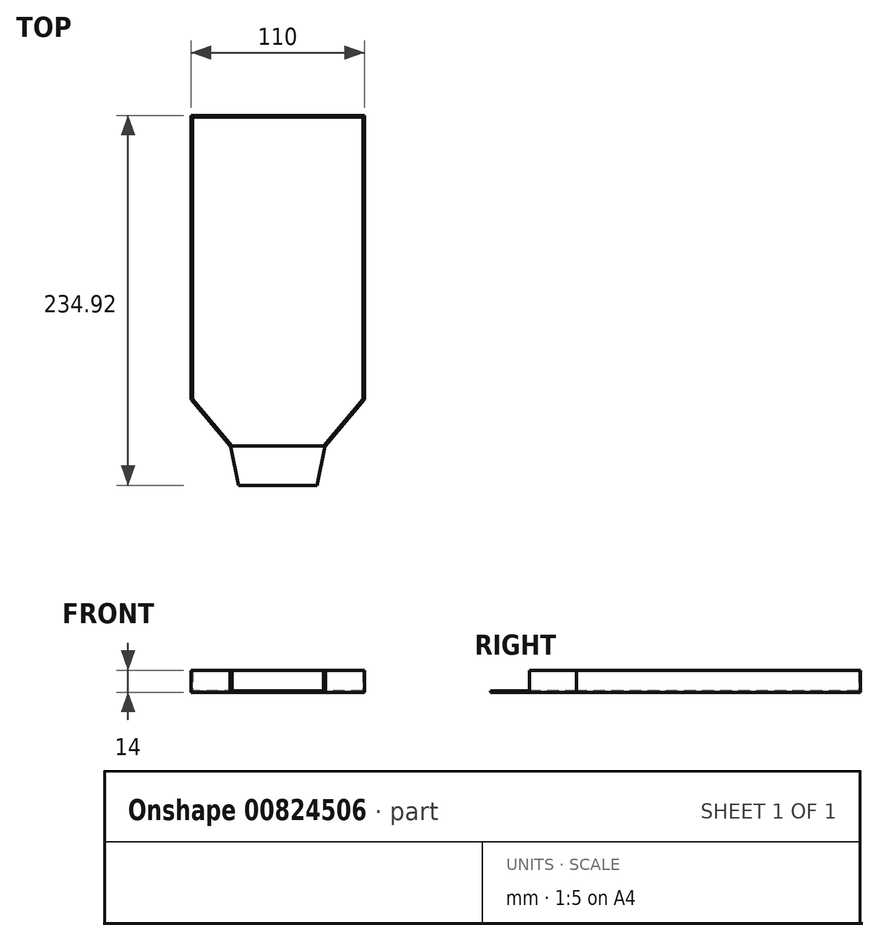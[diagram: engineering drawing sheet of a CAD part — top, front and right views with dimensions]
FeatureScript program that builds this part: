
annotation { "Feature Type Name" : "Feature", "Feature Type Description" : "" }
export const myFeature = defineFeature(function(context is Context, id is Id, definition is map)
    precondition{}
    {
        {
            var Q0;
            Q0=qCreatedBy(makeId("Top.planeOp"),FACE);
            var sketch = newSketch(context, id + "F0", { "sketchPlane" : qUnion([Q0])});
            skLineSegment(sketch, "E0.bottom", {"start": v(-58.97, 116.08) * mm, "end": v(51.03, 116.08) * mm});
            skLineSegment(sketch, "E0.top", {"start": v(-58.97, -93.92) * mm, "end": v(51.03, -93.92) * mm});
            skLineSegment(sketch, "E0.left", {"start": v(-58.97, 116.08) * mm, "end": v(-58.97, -93.92) * mm});
            skLineSegment(sketch, "E0.right", {"start": v(51.03, 116.08) * mm, "end": v(51.03, -93.92) * mm});
            skSolve(sketch);
        }
        {
            var Q0;
            Q0 = qSketchRegion(id + "F0", true);
            extrude(context, id + "F1", {"entities" : qUnion([Q0]), "depth" : 1 * mm, "offsetDistance" : 25 * mm});
        }
        {
            var Q0;
            Q0=makeQuery(id+"F1.opExtrude","CAP_FACE",FACE,{"disambiguationData":[OSD([sQuery(id+"F0.wireOp",EDGE,"E0.bottom"),sQuery(id+"F0.wireOp",EDGE,"E0.top"),sQuery(id+"F0.wireOp",EDGE,"E0.left"),sQuery(id+"F0.wireOp",EDGE,"E0.right")])],"isStart":false});
            var sketch = newSketch(context, id + "F2", { "sketchPlane" : qUnion([Q0])});
            skLineSegment(sketch, "E1.bottom", {"start": v(51.03, 116.08) * mm, "end": v(50.03, 116.08) * mm});
            skLineSegment(sketch, "E1.top", {"start": v(51.03, -93.92) * mm, "end": v(50.03, -93.92) * mm});
            skLineSegment(sketch, "E1.left", {"start": v(51.03, 116.08) * mm, "end": v(51.03, -93.92) * mm});
            skLineSegment(sketch, "E1.right", {"start": v(50.03, 116.08) * mm, "end": v(50.03, -93.92) * mm});
            skSolve(sketch);
        }
        {
            var Q0;
            Q0 = qSketchRegion(id + "F2", true);
            extrude(context, id + "F3", {"entities" : qUnion([Q0]), "operationType" : NewBodyOperationType.ADD, "depth" : 13 * mm, "offsetDistance" : 25 * mm});
        }
        {
            var Q0;
            Q0=makeQuery(id+"F1.opExtrude","CAP_FACE",FACE,{"disambiguationData":[OSD([sQuery(id+"F0.wireOp",EDGE,"E0.bottom"),sQuery(id+"F0.wireOp",EDGE,"E0.top"),sQuery(id+"F0.wireOp",EDGE,"E0.left"),sQuery(id+"F0.wireOp",EDGE,"E0.right")])],"isStart":false});
            var sketch = newSketch(context, id + "F4", { "sketchPlane" : qUnion([Q0])});
            skLineSegment(sketch, "E2.bottom", {"start": v(50.03, 116.08) * mm, "end": v(-58.97, 116.08) * mm});
            skLineSegment(sketch, "E2.top", {"start": v(50.03, 115.08) * mm, "end": v(-58.97, 115.08) * mm});
            skLineSegment(sketch, "E2.left", {"start": v(50.03, 116.08) * mm, "end": v(50.03, 115.08) * mm});
            skLineSegment(sketch, "E2.right", {"start": v(-58.97, 116.08) * mm, "end": v(-58.97, 115.08) * mm});
            skSolve(sketch);
        }
        {
            var Q0;
            Q0 = qSketchRegion(id + "F4", true);
            extrude(context, id + "F5", {"entities" : qUnion([Q0]), "operationType" : NewBodyOperationType.ADD, "depth" : 13 * mm, "offsetDistance" : 25 * mm});
        }
        {
            var Q0;
            Q0=makeQuery(id+"F1.opExtrude","CAP_FACE",FACE,{"disambiguationData":[OSD([sQuery(id+"F0.wireOp",EDGE,"E0.bottom"),sQuery(id+"F0.wireOp",EDGE,"E0.top"),sQuery(id+"F0.wireOp",EDGE,"E0.left"),sQuery(id+"F0.wireOp",EDGE,"E0.right")])],"isStart":false});
            var sketch = newSketch(context, id + "F6", { "sketchPlane" : qUnion([Q0])});
            skLineSegment(sketch, "E3.bottom", {"start": v(-58.97, 115.08) * mm, "end": v(-57.97, 115.08) * mm});
            skLineSegment(sketch, "E3.top", {"start": v(-58.97, -93.92) * mm, "end": v(-57.97, -93.92) * mm});
            skLineSegment(sketch, "E3.left", {"start": v(-58.97, 115.08) * mm, "end": v(-58.97, -93.92) * mm});
            skLineSegment(sketch, "E3.right", {"start": v(-57.97, 115.08) * mm, "end": v(-57.97, -93.92) * mm});
            skSolve(sketch);
        }
        {
            var Q0;
            Q0 = qSketchRegion(id + "F6", true);
            extrude(context, id + "F7", {"entities" : qUnion([Q0]), "operationType" : NewBodyOperationType.ADD, "depth" : 13 * mm, "offsetDistance" : 25 * mm});
        }
        {
            var Q0;
            Q0=makeQuery(id+"F1.opExtrude","CAP_FACE",FACE,{"disambiguationData":[OSD([sQuery(id+"F0.wireOp",EDGE,"E0.bottom"),sQuery(id+"F0.wireOp",EDGE,"E0.top"),sQuery(id+"F0.wireOp",EDGE,"E0.left"),sQuery(id+"F0.wireOp",EDGE,"E0.right")])],"isStart":false});
            var sketch = newSketch(context, id + "F8", { "sketchPlane" : qUnion([Q0])});
            skLineSegment(sketch, "E4", {"start": v(-32.97, -93.92) * mm, "end": v(-57.97, -93.92) * mm});
            skLineSegment(sketch, "E5", {"start": v(-57.97, -93.92) * mm, "end": v(-57.97, -63.92) * mm});
            skLineSegment(sketch, "E6", {"start": v(-57.97, -63.92) * mm, "end": v(-32.97, -93.92) * mm});
            skSolve(sketch);
        }
        {
            var Q0;
            Q0=makeQuery(id+"F8.imprint","IMPRINT",FACE,{"disambiguationData":[TD([[makeQuery(id+"F8.imprint","IMPRINT",EDGE,{"derivedFrom":sQuery(id+"F8.wireOp",EDGE,"E4")}),1.0]])]});
            extrude(context, id + "F9", {"entities" : qUnion([Q0]), "operationType" : NewBodyOperationType.ADD, "depth" : 13 * mm, "offsetDistance" : 25 * mm});
        }
        {
            var Q0;
            Q0=makeQuery(id+"F9.boolean.opBoolean","MERGE",FACE,{"derivedFrom":[makeQuery(id+"F7.boolean.opBoolean","MERGE",FACE,{"derivedFrom":[makeQuery(id+"F5.boolean.opBoolean","MERGE",FACE,{"derivedFrom":[makeQuery(id+"F3.opExtrude","CAP_FACE",FACE,{"disambiguationData":[OSD([sQuery(id+"F2.wireOp",EDGE,"E1.bottom"),sQuery(id+"F2.wireOp",EDGE,"E1.top"),sQuery(id+"F2.wireOp",EDGE,"E1.left"),sQuery(id+"F2.wireOp",EDGE,"E1.right")])],"isStart":false}),makeQuery(id+"F5.opExtrude","CAP_FACE",FACE,{"disambiguationData":[OSD([sQuery(id+"F4.wireOp",EDGE,"E2.bottom"),sQuery(id+"F4.wireOp",EDGE,"E2.top"),sQuery(id+"F4.wireOp",EDGE,"E2.left"),sQuery(id+"F4.wireOp",EDGE,"E2.right")])],"isStart":false})]}),makeQuery(id+"F7.opExtrude","CAP_FACE",FACE,{"disambiguationData":[OSD([sQuery(id+"F6.wireOp",EDGE,"E3.bottom"),sQuery(id+"F6.wireOp",EDGE,"E3.top"),sQuery(id+"F6.wireOp",EDGE,"E3.left"),sQuery(id+"F6.wireOp",EDGE,"E3.right")])],"isStart":false})]}),makeQuery(id+"F9.opExtrude","CAP_FACE",FACE,{"disambiguationData":[OSD([sQuery(id+"F8.wireOp",EDGE,"E4"),sQuery(id+"F8.wireOp",EDGE,"E5"),sQuery(id+"F8.wireOp",EDGE,"E6")])],"isStart":false})]});
            var Q1;
            Q1=makeQuery(id+"F9.boolean.opBoolean","MERGE",FACE,{"derivedFrom":[makeQuery(id+"F7.boolean.opBoolean","MERGE",FACE,{"derivedFrom":[makeQuery(id+"F3.boolean.opBoolean","MERGE",FACE,{"derivedFrom":[makeQuery(id+"F1.opExtrude","SWEPT_FACE",FACE,{"disambiguationData":[OSD([sQuery(id+"F0.wireOp",EDGE,"E0.top")])]}),makeQuery(id+"F3.opExtrude","SWEPT_FACE",FACE,{"disambiguationData":[OSD([sQuery(id+"F2.wireOp",EDGE,"E1.top")])]})]}),makeQuery(id+"F7.opExtrude","SWEPT_FACE",FACE,{"disambiguationData":[OSD([sQuery(id+"F6.wireOp",EDGE,"E3.top")])]})]}),makeQuery(id+"F9.opExtrude","SWEPT_FACE",FACE,{"disambiguationData":[OSD([sQuery(id+"F8.wireOp",EDGE,"E4")])]})]});
            var Q2;
            Q2=makeQuery(id+"F7.boolean.opBoolean","MERGE",FACE,{"derivedFrom":[makeQuery(id+"F5.boolean.opBoolean","MERGE",FACE,{"derivedFrom":[makeQuery(id+"F1.opExtrude","SWEPT_FACE",FACE,{"disambiguationData":[OSD([sQuery(id+"F0.wireOp",EDGE,"E0.left")])]}),makeQuery(id+"F5.opExtrude","SWEPT_FACE",FACE,{"disambiguationData":[OSD([sQuery(id+"F4.wireOp",EDGE,"E2.right")])]})]}),makeQuery(id+"F7.opExtrude","SWEPT_FACE",FACE,{"disambiguationData":[OSD([sQuery(id+"F6.wireOp",EDGE,"E3.left")])]})]});
            var Q3;
            Q3=makeQuery(id+"F1.opExtrude","CAP_FACE",FACE,{"disambiguationData":[OSD([sQuery(id+"F0.wireOp",EDGE,"E0.bottom"),sQuery(id+"F0.wireOp",EDGE,"E0.top"),sQuery(id+"F0.wireOp",EDGE,"E0.left"),sQuery(id+"F0.wireOp",EDGE,"E0.right")])],"isStart":true});
            shell(context, id + "F10", {"entities" : qUnion([Q0, Q1, Q2, Q3]), "thickness" : 1 * mm});
        }
        {
            var Q0;
            Q0=makeQuery(id+"F1.opExtrude","CAP_FACE",FACE,{"disambiguationData":[OSD([sQuery(id+"F0.wireOp",EDGE,"E0.bottom"),sQuery(id+"F0.wireOp",EDGE,"E0.top"),sQuery(id+"F0.wireOp",EDGE,"E0.left"),sQuery(id+"F0.wireOp",EDGE,"E0.right")])],"isStart":true});
            var sketch = newSketch(context, id + "F11", { "sketchPlane" : qUnion([Q0])});
            skSolve(sketch);
        }
        {
            var Q0;
            Q0=makeQuery(id+"F1.opExtrude","CAP_FACE",FACE,{"disambiguationData":[OSD([sQuery(id+"F0.wireOp",EDGE,"E0.bottom"),sQuery(id+"F0.wireOp",EDGE,"E0.top"),sQuery(id+"F0.wireOp",EDGE,"E0.left"),sQuery(id+"F0.wireOp",EDGE,"E0.right")])],"isStart":false});
            var sketch = newSketch(context, id + "F12", { "sketchPlane" : qUnion([Q0])});
            skLineSegment(sketch, "E7", {"start": v(50.03, -93.92) * mm, "end": v(25.03, -93.92) * mm});
            skLineSegment(sketch, "E8", {"start": v(50.03, -93.92) * mm, "end": v(50.03, -63.92) * mm});
            skLineSegment(sketch, "E9", {"start": v(50.03, -63.92) * mm, "end": v(25.03, -93.92) * mm});
            skSolve(sketch);
        }
        {
            var Q0;
            Q0=makeQuery(id+"F12.imprint","IMPRINT",FACE,{"disambiguationData":[TD([[makeQuery(id+"F12.imprint","IMPRINT",EDGE,{"derivedFrom":sQuery(id+"F12.wireOp",EDGE,"E7")}),1.0]])]});
            extrude(context, id + "F13", {"entities" : qUnion([Q0]), "operationType" : NewBodyOperationType.ADD, "depth" : 13 * mm, "offsetDistance" : 25 * mm});
        }
        {
            var Q0;
            Q0=makeQuery(id+"F13.boolean.opBoolean","MERGE",FACE,{"derivedFrom":[makeQuery(id+"F9.boolean.opBoolean","MERGE",FACE,{"derivedFrom":[makeQuery(id+"F7.boolean.opBoolean","MERGE",FACE,{"derivedFrom":[makeQuery(id+"F5.boolean.opBoolean","MERGE",FACE,{"derivedFrom":[makeQuery(id+"F3.opExtrude","CAP_FACE",FACE,{"disambiguationData":[OSD([sQuery(id+"F2.wireOp",EDGE,"E1.bottom"),sQuery(id+"F2.wireOp",EDGE,"E1.top"),sQuery(id+"F2.wireOp",EDGE,"E1.left"),sQuery(id+"F2.wireOp",EDGE,"E1.right")])],"isStart":false}),makeQuery(id+"F5.opExtrude","CAP_FACE",FACE,{"disambiguationData":[OSD([sQuery(id+"F4.wireOp",EDGE,"E2.bottom"),sQuery(id+"F4.wireOp",EDGE,"E2.top"),sQuery(id+"F4.wireOp",EDGE,"E2.left"),sQuery(id+"F4.wireOp",EDGE,"E2.right")])],"isStart":false})]}),makeQuery(id+"F7.opExtrude","CAP_FACE",FACE,{"disambiguationData":[OSD([sQuery(id+"F6.wireOp",EDGE,"E3.bottom"),sQuery(id+"F6.wireOp",EDGE,"E3.top"),sQuery(id+"F6.wireOp",EDGE,"E3.left"),sQuery(id+"F6.wireOp",EDGE,"E3.right")])],"isStart":false})]}),makeQuery(id+"F9.opExtrude","CAP_FACE",FACE,{"disambiguationData":[OSD([sQuery(id+"F8.wireOp",EDGE,"E4"),sQuery(id+"F8.wireOp",EDGE,"E5"),sQuery(id+"F8.wireOp",EDGE,"E6")])],"isStart":false})]}),makeQuery(id+"F13.opExtrude","CAP_FACE",FACE,{"disambiguationData":[OSD([sQuery(id+"F12.wireOp",EDGE,"E7"),sQuery(id+"F12.wireOp",EDGE,"E8"),sQuery(id+"F12.wireOp",EDGE,"E9")])],"isStart":false})]});
            var Q1;
            Q1=makeQuery(id+"F13.boolean.opBoolean","MERGE",FACE,{"derivedFrom":[makeQuery(id+"F9.boolean.opBoolean","MERGE",FACE,{"derivedFrom":[makeQuery(id+"F7.boolean.opBoolean","MERGE",FACE,{"derivedFrom":[makeQuery(id+"F3.boolean.opBoolean","MERGE",FACE,{"derivedFrom":[makeQuery(id+"F1.opExtrude","SWEPT_FACE",FACE,{"disambiguationData":[OSD([sQuery(id+"F0.wireOp",EDGE,"E0.top")])]}),makeQuery(id+"F3.opExtrude","SWEPT_FACE",FACE,{"disambiguationData":[OSD([sQuery(id+"F2.wireOp",EDGE,"E1.top")])]})]}),makeQuery(id+"F7.opExtrude","SWEPT_FACE",FACE,{"disambiguationData":[OSD([sQuery(id+"F6.wireOp",EDGE,"E3.top")])]})]}),makeQuery(id+"F9.opExtrude","SWEPT_FACE",FACE,{"disambiguationData":[OSD([sQuery(id+"F8.wireOp",EDGE,"E4")])]})]}),makeQuery(id+"F13.opExtrude","SWEPT_FACE",FACE,{"disambiguationData":[OSD([sQuery(id+"F12.wireOp",EDGE,"E7")])]})]});
            var Q2;
            Q2=makeQuery(id+"F3.boolean.opBoolean","MERGE",FACE,{"derivedFrom":[makeQuery(id+"F1.opExtrude","SWEPT_FACE",FACE,{"disambiguationData":[OSD([sQuery(id+"F0.wireOp",EDGE,"E0.right")])]}),makeQuery(id+"F3.opExtrude","SWEPT_FACE",FACE,{"disambiguationData":[OSD([sQuery(id+"F2.wireOp",EDGE,"E1.left")])]})]});
            var Q3;
            Q3=makeQuery(id+"F1.opExtrude","CAP_FACE",FACE,{"disambiguationData":[OSD([sQuery(id+"F0.wireOp",EDGE,"E0.bottom"),sQuery(id+"F0.wireOp",EDGE,"E0.top"),sQuery(id+"F0.wireOp",EDGE,"E0.left"),sQuery(id+"F0.wireOp",EDGE,"E0.right")])],"isStart":true});
            shell(context, id + "F14", {"entities" : qUnion([Q0, Q1, Q2, Q3]), "thickness" : 1 * mm});
        }
        {
            var Q0;
            Q0=makeQuery(id+"F11.imprint","IMPRINT",FACE,{"disambiguationData":[TD([[makeQuery(id+"F11.imprint","IMPRINT",EDGE,{"derivedFrom":makeQuery(id+"F1.opExtrude","CAP_EDGE",EDGE,{"disambiguationData":[OSD([sQuery(id+"F0.wireOp",EDGE,"E0.bottom")])],"isStart":true})}),1.0]])]});
            var sketch = newSketch(context, id + "F15", { "sketchPlane" : qUnion([Q0])});
            skLineSegment(sketch, "E10.bottom", {"start": v(-33.96, 93.84) * mm, "end": v(26.04, 93.84) * mm});
            skLineSegment(sketch, "E10.top", {"start": v(-33.96, 118.84) * mm, "end": v(26.04, 118.84) * mm});
            skLineSegment(sketch, "E10.left", {"start": v(-33.96, 93.84) * mm, "end": v(-33.96, 118.84) * mm});
            skLineSegment(sketch, "E10.right", {"start": v(26.04, 93.84) * mm, "end": v(26.04, 118.84) * mm});
            skSolve(sketch);
        }
        {
            var Q0;
            {var subQ0=sQuery(id+"F15.wireOp",EDGE,"E10.top");Q0=makeQuery(id+"F15.imprint","IMPRINT",FACE,{"disambiguationData":[TD([[makeQuery(id+"F15.imprint","IMPRINT",EDGE,{"derivedFrom":subQ0}),-1.0]])]});}
            extrude(context, id + "F16", {"entities" : qUnion([Q0]), "oppositeDirection" : true, "depth" : 1 * mm, "offsetDistance" : 25 * mm});
        }
        {
            var Q0;
            Q0=makeQuery(id+"F16.opExtrude","SWEPT_EDGE",EDGE,{"disambiguationData":[OSD([sQuery(id+"F15.wireOp",EDGE,"E10.top"),sQuery(id+"F15.wireOp",EDGE,"E10.left")])]});
            chamfer(context, id + "F17", {"entities" : qUnion([Q0]), "chamferType" : ChamferType.TWO_OFFSETS, "width1" : 5 * mm, "oppositeDirection" : false, "width2" : 25 * mm, "tangentPropagation" : true});
        }
        {
            var Q0;
            Q0=makeQuery(id+"F16.opExtrude","SWEPT_EDGE",EDGE,{"disambiguationData":[OSD([sQuery(id+"F15.wireOp",EDGE,"E10.top"),sQuery(id+"F15.wireOp",EDGE,"E10.right")])]});
            chamfer(context, id + "F18", {"entities" : qUnion([Q0]), "chamferType" : ChamferType.TWO_OFFSETS, "width1" : 25 * mm, "oppositeDirection" : false, "width2" : 5 * mm, "tangentPropagation" : true});
        }
    });
